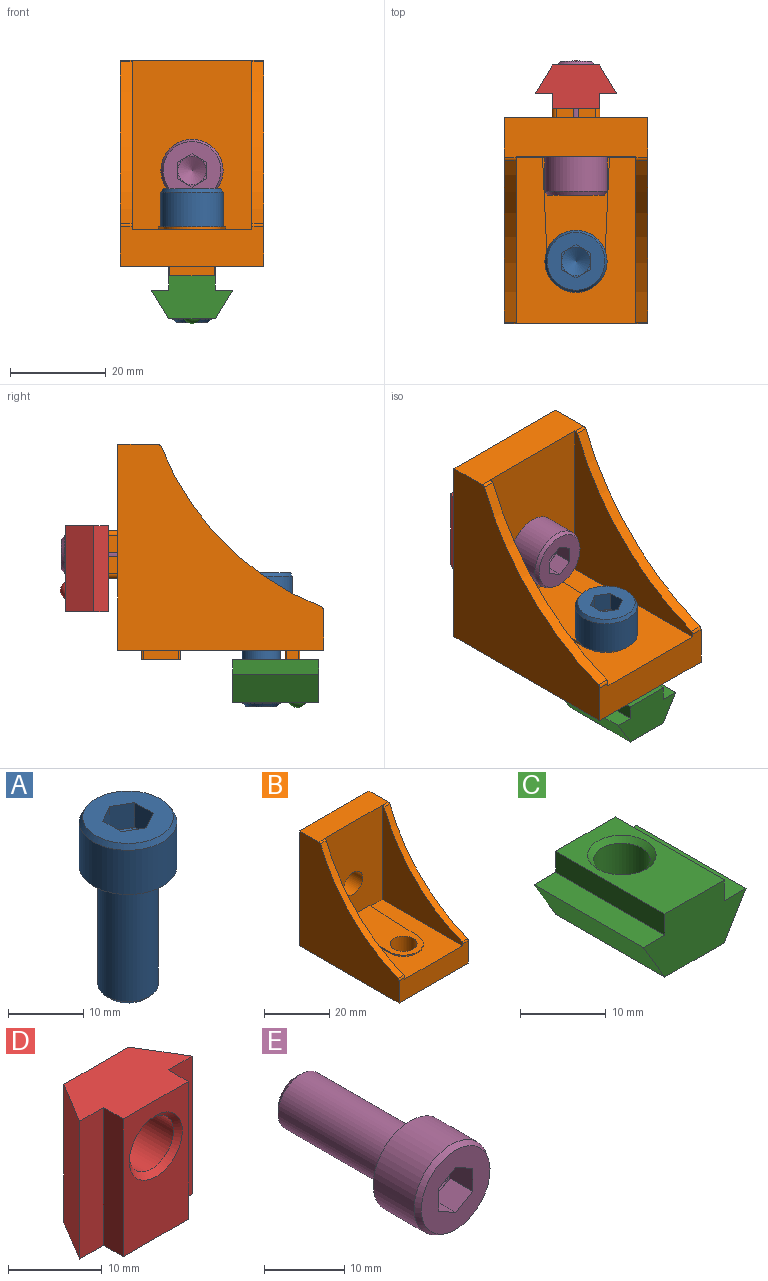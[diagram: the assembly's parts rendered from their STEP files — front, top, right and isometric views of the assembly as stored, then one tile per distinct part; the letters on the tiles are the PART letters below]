
ASSEMBLY  parts=5 mates=6
PART A: 21 faces, bbox 13x13x28 mm
  f0: cone r=6.04mm half-angle=30deg, axis (0,0,-1), area 36.4mm2, adj f1,f14
  f1: plane 12.08x12.08mm, normal (0,0,1), area 83.4mm2, adj f0,f2,f3,f4,f5,f6,f7
  f2: plane 4x3mm, normal (-0.5,0.87,0), area 13.9mm2, adj f1,f3,f4,f17,f18
  f3: plane 4x3mm, normal (0.5,0.87,0), area 13.9mm2, adj f1,f2,f7,f18,f19
  f4: plane 4x3.46mm, normal (-1,0,0), area 13.9mm2, adj f1,f2,f5,f15,f17
  f5: plane 4x3mm, normal (-0.5,-0.87,0), area 13.9mm2, adj f1,f4,f6,f15,f16
  f6: plane 4x3mm, normal (0.5,-0.87,0), area 13.9mm2, adj f1,f5,f7,f16,f20
  f7: plane 4x3.46mm, normal (1,0,0), area 13.9mm2, adj f1,f3,f6,f19,f20
  f8: cone r=3mm half-angle=60deg, axis (0,0,1), area 32.6mm2, adj f15,f16,f17,f18,f19,f20
  f9: plane 6.47x6.47mm, normal (0,0,-1), area 32.8mm2, adj f10
  f10: cone r=4mm half-angle=45deg, axis (0,0,1), area 24.6mm2, adj f9,f11
  f11: cylinder r=4mm len=18.83mm, axis (0,0,1), area 473.3mm2, adj f10,f12
  f12: torus R=4.4mm, axis (0,0,-1), area 16.4mm2, adj f11,f13
  f13: plane 13x13mm, normal (0,0,-1), area 71.9mm2, adj f12,f14
  f14: cylinder r=6.5mm len=13mm, axis (0,0,1), area 294.1mm2, adj f0,f13
  f15: plane 2.6x1.5mm, normal (0,0,1), area 0.5mm2, adj f4,f5,f8
  f16: plane 3x0.87mm, normal (0,0,1), area 0.5mm2, adj f5,f6,f8
  f17: plane 2.6x1.5mm, normal (0,0,1), area 0.5mm2, adj f2,f4,f8
  f18: plane 3x0.87mm, normal (0,0,1), area 0.5mm2, adj f2,f3,f8
  f19: plane 2.6x1.5mm, normal (0,0,1), area 0.5mm2, adj f3,f7,f8
  f20: plane 2.6x1.5mm, normal (0,0,1), area 0.5mm2, adj f6,f7,f8
PART B: 64 faces, bbox 30x45x45 mm
  f0: cylinder r=59.33mm len=33.71mm, axis (1,0,0), area 122.7mm2, adj f5,f7,f10,f13
  f1: plane 22.07x1.01mm, normal (-1,-0.05,0), area 11mm2, adj f3,f4,f17,f19
  f2: cylinder r=59.33mm len=33.71mm, axis (1,0,0), area 122.7mm2, adj f6,f11,f12,f14
  f3: plane 34.8x25mm, normal (0,0,1), area 529.9mm2, adj f1,f4,f9,f13,f14,f18,f19
  f4: plane 35.3x25mm, normal (0,-1,0), area 822.7mm2, adj f1,f3,f8,f13,f14,f15,f17,f18
  f5: plane 43x43mm, normal (1,0,0), area 1100.4mm2, adj f0,f7,f8,f9,f10,f37,f59
  f6: plane 43x43mm, normal (-1,0,0), area 1100.4mm2, adj f2,f8,f9,f11,f12,f37,f59
  f7: cylinder r=1mm len=2.5mm, axis (1,0,0), area 2mm2, adj f0,f5,f8,f13
  f8: plane 30x8.29mm, normal (0,0,1), area 246.4mm2, adj f4,f5,f6,f7,f11,f13,f14,f59
  f9: plane 30x8.29mm, normal (0,-1,0), area 233.9mm2, adj f3,f5,f6,f10,f12,f13,f14,f37
  f10: cylinder r=1mm len=2.5mm, axis (1,0,0), area 2mm2, adj f0,f5,f9,f13
  f11: cylinder r=1mm len=2.5mm, axis (1,0,0), area 2mm2, adj f2,f6,f8,f14
  f12: cylinder r=1mm len=2.5mm, axis (1,0,0), area 2mm2, adj f2,f6,f9,f14
  f13: plane 35.3x34.8mm, normal (-1,0,0), area 479.8mm2, adj f0,f3,f4,f7,f8,f9,f10
  f14: plane 35.3x34.8mm, normal (1,0,0), area 479.8mm2, adj f2,f3,f4,f8,f9,f11,f12
  f15: cylinder r=4.1mm len=10.2mm, axis (0,-1,0), area 254.7mm2, adj f4,f38,f39,f43,f44,f48,f50,f51
  f16: cylinder r=4.1mm len=8.2mm, axis (0,0,1), area 211.2mm2, adj f17,f37
  f17: plane 27.8x14mm, normal (0,0,1), area 287.3mm2, adj f1,f4,f16,f18,f19
  f18: plane 22.07x1.01mm, normal (1,-0.05,0), area 11mm2, adj f3,f4,f17,f19
  f19: cylinder r=6mm len=11.99mm, axis (0,0,1), area 9.2mm2, adj f1,f3,f17,f18
  f20: plane 10x3mm, normal (0,0,-1), area 29.9mm2, adj f21,f22,f23,f24,f25,f26,f27,f28
  f21: plane 2.4x2mm, normal (-1,0,0), area 4.8mm2, adj f20,f22,f28,f37
  f22: cylinder r=0.3mm len=2mm, axis (0,0,-1), area 0.9mm2, adj f20,f21,f23,f37
  f23: plane 9.4x2mm, normal (0,-1,0), area 18.8mm2, adj f20,f22,f24,f37
  f24: cylinder r=0.3mm len=2mm, axis (0,0,-1), area 0.9mm2, adj f20,f23,f25,f37
  f25: plane 2.4x2mm, normal (1,0,0), area 4.8mm2, adj f20,f24,f26,f37
  f26: cylinder r=0.3mm len=2mm, axis (0,0,-1), area 0.9mm2, adj f20,f25,f27,f37
  f27: plane 9.4x2mm, normal (0,1,0), area 18.8mm2, adj f20,f26,f28,f37
  f28: cylinder r=0.3mm len=2mm, axis (0,0,-1), area 0.9mm2, adj f20,f21,f27,f37
  f29: plane 7.4x2mm, normal (-1,0,0), area 14.8mm2, adj f30,f36,f37,f60
  f30: cylinder r=0.3mm len=2mm, axis (0,0,-1), area 0.9mm2, adj f29,f31,f37,f60
  f31: plane 9.4x2mm, normal (0,-1,0), area 18.8mm2, adj f30,f32,f37,f60
  f32: cylinder r=0.3mm len=2mm, axis (0,0,-1), area 0.9mm2, adj f31,f33,f37,f60
  f33: plane 7.4x2mm, normal (1,0,0), area 14.8mm2, adj f32,f34,f37,f60
  f34: cylinder r=0.3mm len=2mm, axis (0,0,-1), area 0.9mm2, adj f33,f35,f37,f60
  f35: plane 9.4x2mm, normal (0,1,0), area 18.8mm2, adj f34,f36,f37,f60
  f36: cylinder r=0.3mm len=2mm, axis (0,0,-1), area 0.9mm2, adj f29,f35,f37,f60
  f37: plane 43x30mm, normal (0,0,-1), area 1127.3mm2, adj f5,f6,f9,f16,f21,f22,f23,f24
  f38: plane 4.5x4.5mm, normal (0,1,0), area 10.7mm2, adj f15,f39,f40,f41,f42,f43
  f39: plane 2x0.93mm, normal (0,0,-1), area 1.9mm2, adj f15,f38,f40,f59
  f40: plane 3.5x2mm, normal (1,0,0), area 7mm2, adj f38,f39,f41,f59
  f41: cylinder r=1mm len=2mm, axis (0,1,0), area 3.1mm2, adj f38,f40,f42,f59
  f42: plane 3.5x2mm, normal (0,0,1), area 7mm2, adj f38,f41,f43,f59
  f43: plane 2x0.93mm, normal (-1,0,0), area 1.9mm2, adj f15,f38,f42,f59
  f44: plane 2x0.93mm, normal (-1,0,0), area 1.9mm2, adj f15,f45,f59,f63
  f45: plane 3.5x2mm, normal (0,0,-1), area 7mm2, adj f44,f46,f59,f63
  f46: cylinder r=1mm len=2mm, axis (0,1,0), area 3.1mm2, adj f45,f47,f59,f63
  f47: plane 3.5x2mm, normal (1,0,0), area 7mm2, adj f46,f48,f59,f63
  f48: plane 2x0.93mm, normal (0,0,1), area 1.9mm2, adj f15,f47,f59,f63
  f49: plane 3.5x2mm, normal (-1,0,0), area 7mm2, adj f50,f53,f59,f61
  f50: plane 2x0.93mm, normal (0,0,-1), area 1.9mm2, adj f15,f49,f59,f61
  f51: plane 2x0.93mm, normal (1,0,0), area 1.9mm2, adj f15,f52,f59,f61
  f52: plane 3.5x2mm, normal (0,0,1), area 7mm2, adj f51,f53,f59,f61
  f53: cylinder r=1mm len=2mm, axis (0,1,0), area 3.1mm2, adj f49,f52,f59,f61
  f54: plane 3.5x2mm, normal (-1,0,0), area 7mm2, adj f55,f58,f59,f62
  f55: cylinder r=1mm len=2mm, axis (0,1,0), area 3.1mm2, adj f54,f56,f59,f62
  f56: plane 3.5x2mm, normal (0,0,-1), area 7mm2, adj f55,f57,f59,f62
  f57: plane 2x0.93mm, normal (1,0,0), area 1.9mm2, adj f15,f56,f59,f62
  f58: plane 2x0.93mm, normal (0,0,1), area 1.9mm2, adj f15,f54,f59,f62
  f59: plane 43x30mm, normal (0,1,0), area 1194.5mm2, adj f5,f6,f8,f15,f37,f39,f40,f41
  f60: plane 10x8mm, normal (0,0,-1), area 79.9mm2, adj f29,f30,f31,f32,f33,f34,f35,f36
  f61: plane 4.5x4.5mm, normal (0,1,0), area 10.7mm2, adj f15,f49,f50,f51,f52,f53
  f62: plane 4.5x4.5mm, normal (0,1,0), area 10.7mm2, adj f15,f54,f55,f56,f57,f58
  f63: plane 4.5x4.5mm, normal (0,1,0), area 10.7mm2, adj f15,f44,f45,f46,f47,f48
PART C: 16 faces, bbox 17x18x10 mm
  f0: plane 18x9.8mm, normal (0,0,-1), area 112.9mm2, adj f1,f7,f8,f9,f10,f13
  f1: plane 18x6mm, normal (-0.86,0,-0.51), area 125.9mm2, adj f0,f2,f8,f9
  f2: plane 18x3.6mm, normal (0,0,1), area 64.8mm2, adj f1,f3,f8,f9
  f3: plane 18x3mm, normal (-1,0,0), area 54mm2, adj f2,f4,f8,f9
  f4: plane 18x9.8mm, normal (0,0,1), area 126.1mm2, adj f3,f5,f8,f9,f12
  f5: plane 18x3mm, normal (1,0,0), area 54mm2, adj f4,f6,f8,f9
  f6: plane 18x3.6mm, normal (0,0,1), area 64.8mm2, adj f5,f7,f8,f9
  f7: plane 18x6mm, normal (0.86,0,-0.51), area 125.9mm2, adj f0,f6,f8,f9
  f8: plane 17x9mm, normal (0,-1,0), area 109.8mm2, adj f0,f1,f2,f3,f4,f5,f6,f7
  f9: plane 17x9mm, normal (0,1,0), area 109.8mm2, adj f0,f1,f2,f3,f4,f5,f6,f7
  f10: cone r=4mm half-angle=45deg, axis (0,0,-1), area 22mm2, adj f0,f11
  f11: cylinder r=3.32mm len=7.65mm, axis (0,0,-1), area 159.7mm2, adj f10,f12
  f12: cone r=3.32mm half-angle=45deg, axis (0,0,1), area 22mm2, adj f4,f11
  f13: cylinder r=2.05mm len=4.1mm, axis (0,0,-1), area 12.9mm2, adj f0,f14
  f14: plane 4.1x4.1mm, normal (0,0,-1), area 0.6mm2, adj f13,f15
  f15: sphere r=2mm, area 25.1mm2, adj f14
PART D: 16 faces, bbox 17x10x18 mm
  f0: plane 18x9.8mm, normal (0,1,0), area 112.9mm2, adj f1,f7,f8,f9,f10,f13
  f1: plane 18x6mm, normal (-0.86,0.51,0), area 125.9mm2, adj f0,f2,f8,f9
  f2: plane 18x3.6mm, normal (0,-1,0), area 64.8mm2, adj f1,f3,f8,f9
  f3: plane 18x3mm, normal (-1,0,0), area 54mm2, adj f2,f4,f8,f9
  f4: plane 18x9.8mm, normal (0,-1,0), area 126.1mm2, adj f3,f5,f8,f9,f12
  f5: plane 18x3mm, normal (1,0,0), area 54mm2, adj f4,f6,f8,f9
  f6: plane 18x3.6mm, normal (0,-1,0), area 64.8mm2, adj f5,f7,f8,f9
  f7: plane 18x6mm, normal (0.86,0.51,0), area 125.9mm2, adj f0,f6,f8,f9
  f8: plane 17x9mm, normal (0,0,-1), area 109.8mm2, adj f0,f1,f2,f3,f4,f5,f6,f7
  f9: plane 17x9mm, normal (0,0,1), area 109.8mm2, adj f0,f1,f2,f3,f4,f5,f6,f7
  f10: cone r=4mm half-angle=45deg, axis (0,1,0), area 22mm2, adj f0,f11
  f11: cylinder r=3.32mm len=7.65mm, axis (0,1,0), area 159.7mm2, adj f10,f12
  f12: cone r=3.32mm half-angle=45deg, axis (0,-1,0), area 22mm2, adj f4,f11
  f13: cylinder r=2.05mm len=4.1mm, axis (0,1,0), area 12.9mm2, adj f0,f14
  f14: plane 4.1x4.1mm, normal (0,1,0), area 0.6mm2, adj f13,f15
  f15: sphere r=2mm, area 25.1mm2, adj f14
PART E: 21 faces, bbox 13x28x13 mm
  f0: cone r=6.04mm half-angle=30deg, axis (0,1,0), area 36.4mm2, adj f1,f14
  f1: plane 12.08x12.08mm, normal (0,-1,0), area 83.4mm2, adj f0,f2,f3,f4,f5,f6,f7
  f2: plane 4x3mm, normal (-0.5,0,0.87), area 13.9mm2, adj f1,f3,f4,f17,f18
  f3: plane 4x3mm, normal (0.5,0,0.87), area 13.9mm2, adj f1,f2,f7,f18,f19
  f4: plane 4x3.46mm, normal (-1,0,0), area 13.9mm2, adj f1,f2,f5,f15,f17
  f5: plane 4x3mm, normal (-0.5,0,-0.87), area 13.9mm2, adj f1,f4,f6,f15,f16
  f6: plane 4x3mm, normal (0.5,0,-0.87), area 13.9mm2, adj f1,f5,f7,f16,f20
  f7: plane 4x3.46mm, normal (1,0,0), area 13.9mm2, adj f1,f3,f6,f19,f20
  f8: cone r=3mm half-angle=60deg, axis (0,-1,0), area 32.6mm2, adj f15,f16,f17,f18,f19,f20
  f9: plane 6.47x6.47mm, normal (0,1,0), area 32.8mm2, adj f10
  f10: cone r=4mm half-angle=45deg, axis (0,-1,0), area 24.6mm2, adj f9,f11
  f11: cylinder r=4mm len=18.83mm, axis (0,-1,0), area 473.3mm2, adj f10,f12
  f12: torus R=4.4mm, axis (0,1,0), area 16.4mm2, adj f11,f13
  f13: plane 13x13mm, normal (0,1,0), area 71.9mm2, adj f12,f14
  f14: cylinder r=6.5mm len=13mm, axis (0,-1,0), area 294.1mm2, adj f0,f13
  f15: plane 2.6x1.5mm, normal (0,-1,0), area 0.5mm2, adj f4,f5,f8
  f16: plane 3x0.87mm, normal (0,-1,0), area 0.5mm2, adj f5,f6,f8
  f17: plane 2.6x1.5mm, normal (0,-1,0), area 0.5mm2, adj f2,f4,f8
  f18: plane 3x0.87mm, normal (0,-1,0), area 0.5mm2, adj f2,f3,f8
  f19: plane 2.6x1.5mm, normal (0,-1,0), area 0.5mm2, adj f3,f7,f8
  f20: plane 2.6x1.5mm, normal (0,-1,0), area 0.5mm2, adj f6,f7,f8
PLACE A t=(-14.6,18.05,-6.65)mm
PLACE B t=(-14.6,18.05,-6.65)mm
PLACE C t=(-14.6,18.05,-6.15)mm
PLACE D t=(-14.6,17.55,-6.65)mm
PLACE E t=(-14.6,18.05,-6.65)mm
MATE fastened E.f11 <-> B.f15  axis (0,1,0) through (-14.6,9.85,13.35)mm
MATE cylindrical D.f10 <-> E.f11  axis (0,-1,0) through (-14.6,20.05,13.35)mm
MATE parallel D.f4 <-> B.f38  axis (0,-1,0) through (-14.6,20.05,19.35)mm
MATE parallel C.f4 <-> B.f20  axis (0,0,1) through (-14.6,-23.95,-8.65)mm
MATE cylindrical C.f10 <-> A.f11  axis (0,0,1) through (-14.6,-11.95,-8.65)mm
MATE fastened A.f11 <-> B.f16  axis (0,0,-1) through (-14.6,-11.95,1.55)mm
